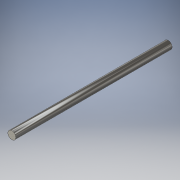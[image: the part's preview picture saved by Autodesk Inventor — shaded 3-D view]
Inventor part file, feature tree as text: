
AUTODESK INVENTOR PART (.ipt)
format: ipt  version: 2019 (Build 230136000, 136)  size: 99,840 bytes
history: native  units: mm
features: other x1, extrude x1, sketch x1
ambient origin geometry x8: Origin, YZ Plane, XZ Plane, XY Plane, X Axis, Y Axis, Z Axis, Center Point
bodies: Body1 (feature_tree)
feature tree (3):
  other  "Твердое тело1"
  extrude  "Выдавливание1"  Depth=6.0mm
  sketch  "Эскиз1"
